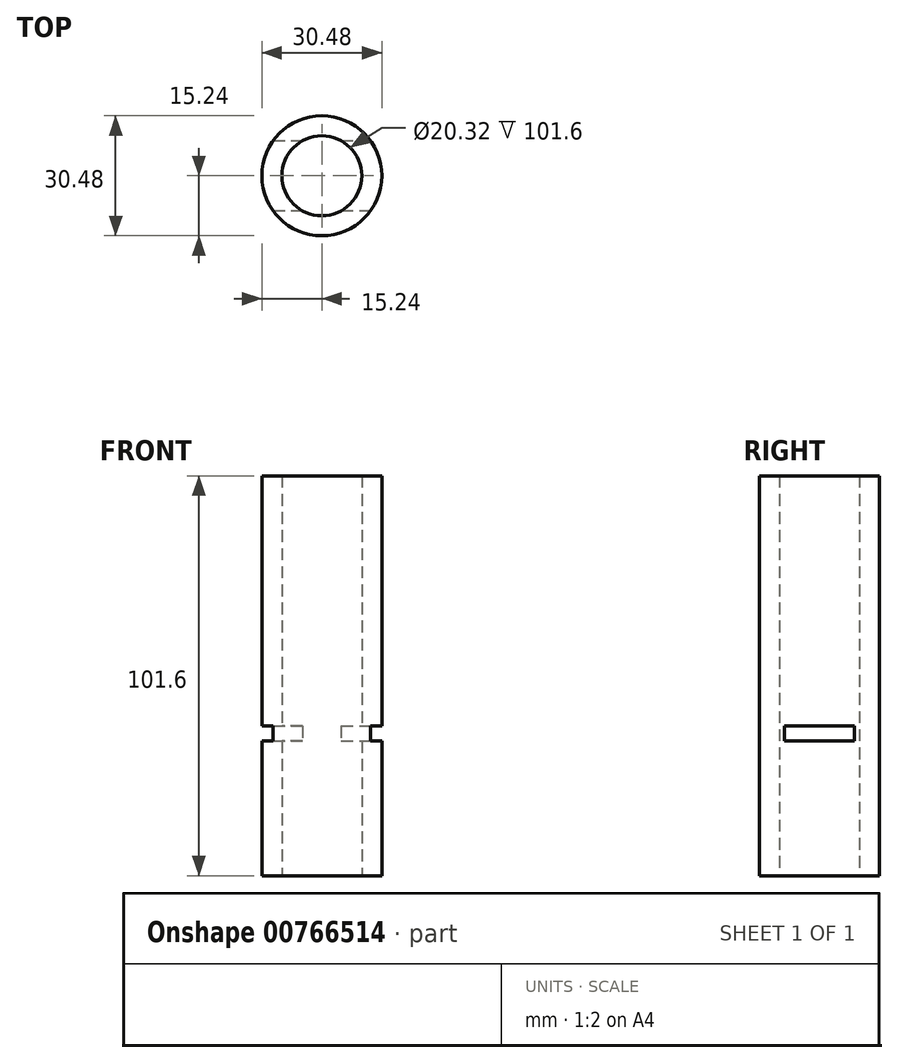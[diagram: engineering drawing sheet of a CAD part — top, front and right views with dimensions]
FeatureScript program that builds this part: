
annotation { "Feature Type Name" : "Feature", "Feature Type Description" : "" }
export const myFeature = defineFeature(function(context is Context, id is Id, definition is map)
    precondition{}
    {
        {
            var Q0;
            Q0=qCreatedBy(makeId("Top.planeOp"),FACE);
            var sketch = newSketch(context, id + "F0", { "sketchPlane" : qUnion([Q0])});
            skCircle(sketch, "E0", {"center": v(0, 0) * mm, "radius": 10.16 * mm});
            skCircle(sketch, "E1", {"center": v(0, 0) * mm, "radius": 15.24 * mm});
            skSolve(sketch);
        }
        {
            var Q0;
            Q0=qSketchRegion(id+"F0",true);
            extrude(context, id + "F1", {"entities" : qUnion([Q0]), "depth" : 101.6 * mm, "offsetDistance" : 25.4 * mm});
        }
        {
            var Q0;
            Q0=qCreatedBy(makeId("Right.planeOp"),FACE);
            var sketch = newSketch(context, id + "F2", { "sketchPlane" : qUnion([Q0])});
            skLineSegment(sketch, "E2", {"start": v(0, 0) * mm, "end": v(0, 34.24) * mm});
            skLineSegment(sketch, "E3", {"start": v(0, 34.24) * mm, "end": v(8.9, 34.24) * mm});
            skLineSegment(sketch, "E4", {"start": v(8.9, 34.24) * mm, "end": v(8.9, 38.05) * mm});
            skLineSegment(sketch, "E5", {"start": v(8.9, 38.05) * mm, "end": v(-8.9, 38.05) * mm});
            skLineSegment(sketch, "E6", {"start": v(-8.9, 38.05) * mm, "end": v(-8.9, 34.24) * mm});
            skLineSegment(sketch, "E7", {"start": v(-8.9, 34.24) * mm, "end": v(0, 34.24) * mm});
            skSolve(sketch);
        }
        {
            var Q0;
            Q0=qSketchRegion(id+"F2",true);
            extrude(context, id + "F3", {"entities" : qUnion([Q0]), "endBound" : BoundingType.SYMMETRIC, "oppositeDirection" : true, "depth" : 76.2 * mm, "offsetDistance" : 25.4 * mm});
        }
        {
            var Q0;
            Q0=makeQuery(id+"F3.opExtrude","SWEPT_BODY",BODY,{"disambiguationData":[OSD([sQuery(id+"F2.wireOp",EDGE,"E3"),sQuery(id+"F2.wireOp",EDGE,"E4"),sQuery(id+"F2.wireOp",EDGE,"E5"),sQuery(id+"F2.wireOp",EDGE,"E6"),sQuery(id+"F2.wireOp",EDGE,"E7")])]});
            var Q1;
            Q1=makeQuery(id+"F1.opExtrude","SWEPT_BODY",BODY,{"disambiguationData":[OSD([sQuery(id+"F0.wireOp",EDGE,"E0"),sQuery(id+"F0.wireOp",EDGE,"E1")])]});
            booleanBodies(context, id + "F4", {"operationType" : BooleanOperationType.SUBTRACTION, "tools" : qUnion([Q0]), "targets" : qUnion([Q1])});
        }
    });
